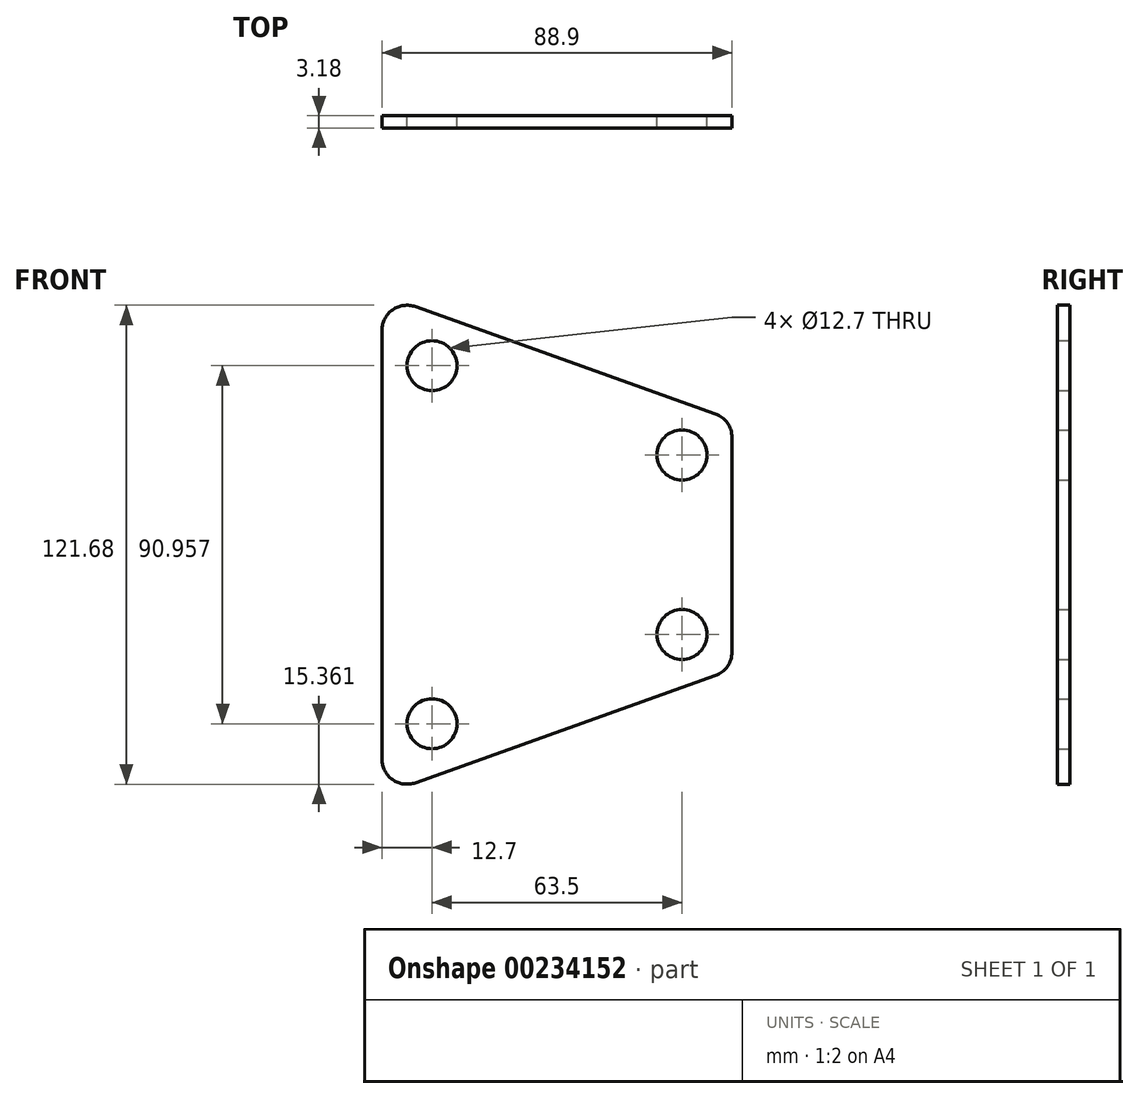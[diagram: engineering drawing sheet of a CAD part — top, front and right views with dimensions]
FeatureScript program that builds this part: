
annotation { "Feature Type Name" : "Feature", "Feature Type Description" : "" }
export const myFeature = defineFeature(function(context is Context, id is Id, definition is map)
    precondition{}
    {
        {
            var Q0;
            Q0=qCreatedBy(makeId("Front.planeOp"),FACE);
            var sketch = newSketch(context, id + "F0", { "sketchPlane" : qUnion([Q0])});
            skLineSegment(sketch, "E0", {"start": v(-44.45, 0) * mm, "end": v(-44.45, 54.49) * mm});
            skLineSegment(sketch, "E1", {"start": v(-35.96, 60.47) * mm, "end": v(40.24, 33.26) * mm});
            skLineSegment(sketch, "E2", {"start": v(44.45, 27.28) * mm, "end": v(44.45, 0) * mm});
            skLineSegment(sketch, "E3.MirrorCS", {"start": v(-44.45, 0) * mm, "end": v(-44.45, -54.49) * mm});
            skLineSegment(sketch, "E4.MirrorCS", {"start": v(-35.96, -60.47) * mm, "end": v(40.24, -33.26) * mm});
            skLineSegment(sketch, "E5.MirrorCS", {"start": v(44.45, -27.28) * mm, "end": v(44.45, 0) * mm});
            skPoint(sketch, "E6", {"position": v(-31.75, 45.48) * mm});
            skPoint(sketch, "E7", {"position": v(31.75, 22.8) * mm});
            skPoint(sketch, "E8.MirrorP", {"position": v(31.75, -22.8) * mm});
            skPoint(sketch, "E9.MirrorP", {"position": v(-31.75, -45.48) * mm});
            skCircle(sketch, "E10", {"center": v(-31.75, 45.48) * mm, "radius": 6.35 * mm});
            skCircle(sketch, "E11", {"center": v(31.75, 22.8) * mm, "radius": 6.35 * mm});
            skCircle(sketch, "E12.MirrorC", {"center": v(31.75, -22.8) * mm, "radius": 6.35 * mm});
            skCircle(sketch, "E13.MirrorC", {"center": v(-31.75, -45.48) * mm, "radius": 6.35 * mm});
            skPoint(sketch, "E14.visualSharp", {"position": v(-44.45, 63.5) * mm});
            skArc(sketch, "E14.filletArc", {"start": v(-35.96, 60.47) * mm, "mid": v(-41.76, 59.68) * mm, "end": v(-44.45, 54.49) * mm});
            skPoint(sketch, "E15.visualSharp", {"position": v(44.45, 31.75) * mm});
            skArc(sketch, "E15.filletArc", {"start": v(44.45, 27.28) * mm, "mid": v(43.3, 30.93) * mm, "end": v(40.24, 33.26) * mm});
            skPoint(sketch, "E16.visualSharp", {"position": v(44.45, -31.75) * mm});
            skArc(sketch, "E16.filletArc", {"start": v(40.24, -33.26) * mm, "mid": v(43.3, -30.93) * mm, "end": v(44.45, -27.28) * mm});
            skPoint(sketch, "E17.visualSharp", {"position": v(-44.45, -63.5) * mm});
            skArc(sketch, "E17.filletArc", {"start": v(-44.45, -54.49) * mm, "mid": v(-41.76, -59.68) * mm, "end": v(-35.96, -60.47) * mm});
            skSolve(sketch);
        }
        {
            var Q0;
            Q0 = qSketchRegion(id + "F0", true);
            extrude(context, id + "F1", {"entities" : qUnion([Q0]), "depth" : 3.17 * mm, "symmetric" : true});
        }
    });
